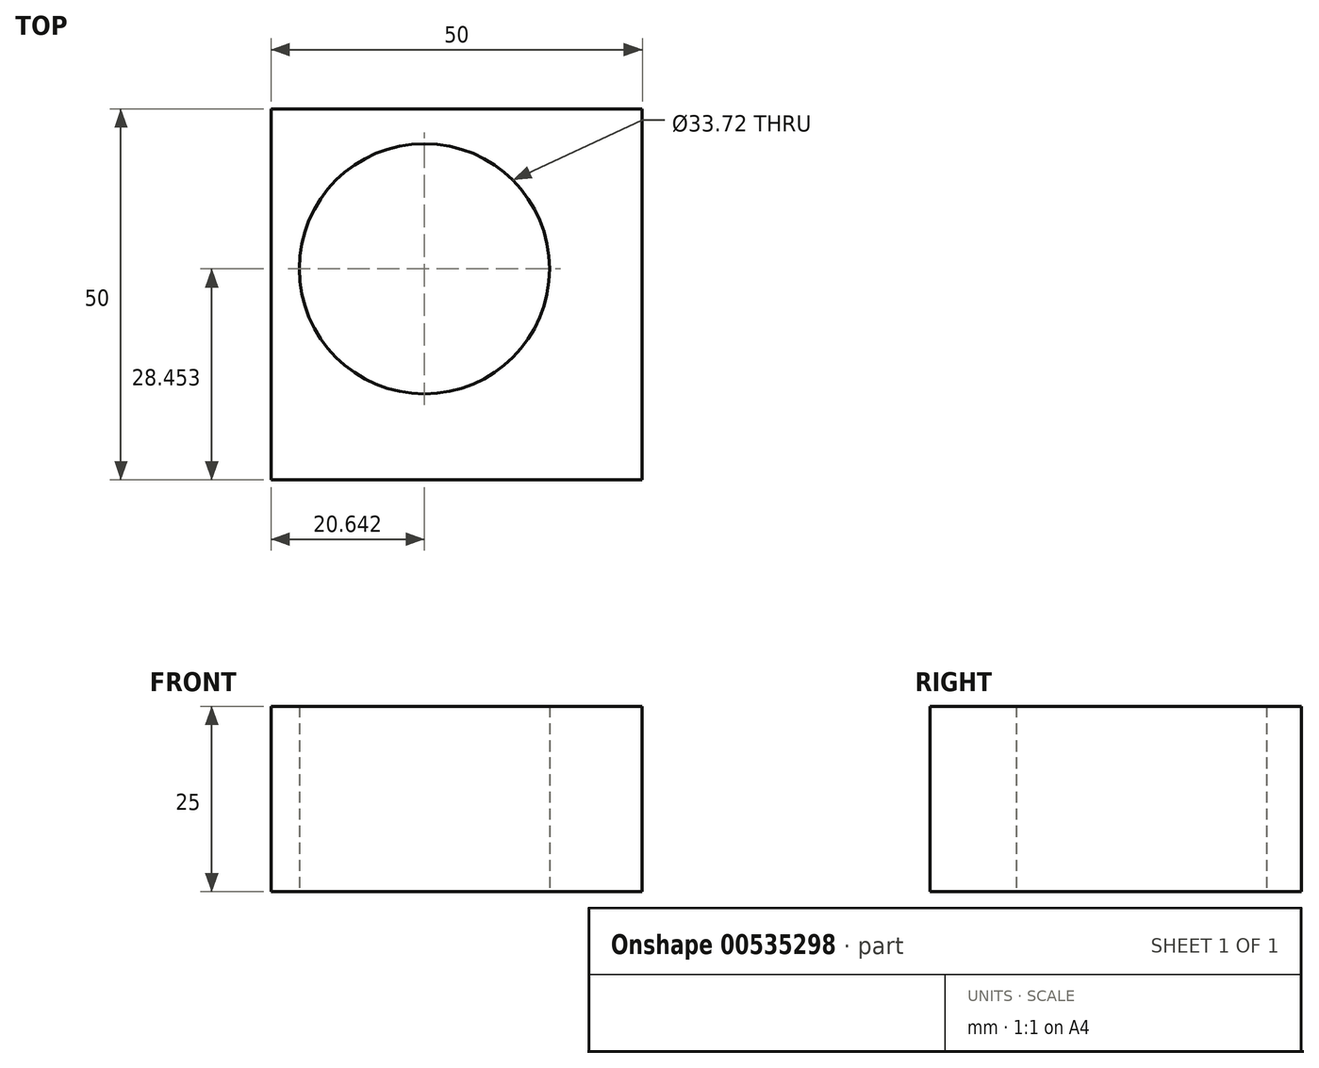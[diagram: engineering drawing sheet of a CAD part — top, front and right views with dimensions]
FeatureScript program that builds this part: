
annotation { "Feature Type Name" : "Feature", "Feature Type Description" : "" }
export const myFeature = defineFeature(function(context is Context, id is Id, definition is map)
    precondition{}
    {
        {
            var Q0;
            Q0=qCreatedBy(makeId("Top.planeOp"),FACE);
            var sketch = newSketch(context, id + "F0", { "sketchPlane" : qUnion([Q0])});
            skLineSegment(sketch, "E0.bottom", {"start": v(4.13, 2.3) * mm, "end": v(54.13, 2.3) * mm});
            skLineSegment(sketch, "E0.top", {"start": v(4.13, -47.7) * mm, "end": v(54.13, -47.7) * mm});
            skLineSegment(sketch, "E0.left", {"start": v(4.13, 2.3) * mm, "end": v(4.13, -47.7) * mm});
            skLineSegment(sketch, "E0.right", {"start": v(54.13, 2.3) * mm, "end": v(54.13, -47.7) * mm});
            skSolve(sketch);
        }
        {
            var Q0;
            Q0 = qSketchRegion(id + "F0", true);
            extrude(context, id + "F1", {"entities" : qUnion([Q0]), "depth" : 25 * mm, "offsetDistance" : 25 * mm});
        }
        {
            var Q0;
            Q0=makeQuery(id+"F1.opExtrude","CAP_FACE",FACE,{"disambiguationData":[OSD([sQuery(id+"F0.wireOp",EDGE,"E0.bottom"),sQuery(id+"F0.wireOp",EDGE,"E0.top"),sQuery(id+"F0.wireOp",EDGE,"E0.left"),sQuery(id+"F0.wireOp",EDGE,"E0.right")])],"isStart":true});
            var sketch = newSketch(context, id + "F2", { "sketchPlane" : qUnion([Q0])});
            skCircle(sketch, "E1", {"center": v(24.77, 19.25) * mm, "radius": 16.86 * mm});
            skSolve(sketch);
        }
        {
            var Q0;
            Q0 = qSketchRegion(id + "F2", true);
            extrude(context, id + "F3", {"entities" : qUnion([Q0]), "operationType" : NewBodyOperationType.REMOVE, "endBound" : BoundingType.UP_TO_NEXT, "oppositeDirection" : true, "depth" : 19 * mm, "offsetDistance" : 25 * mm});
        }
    });
